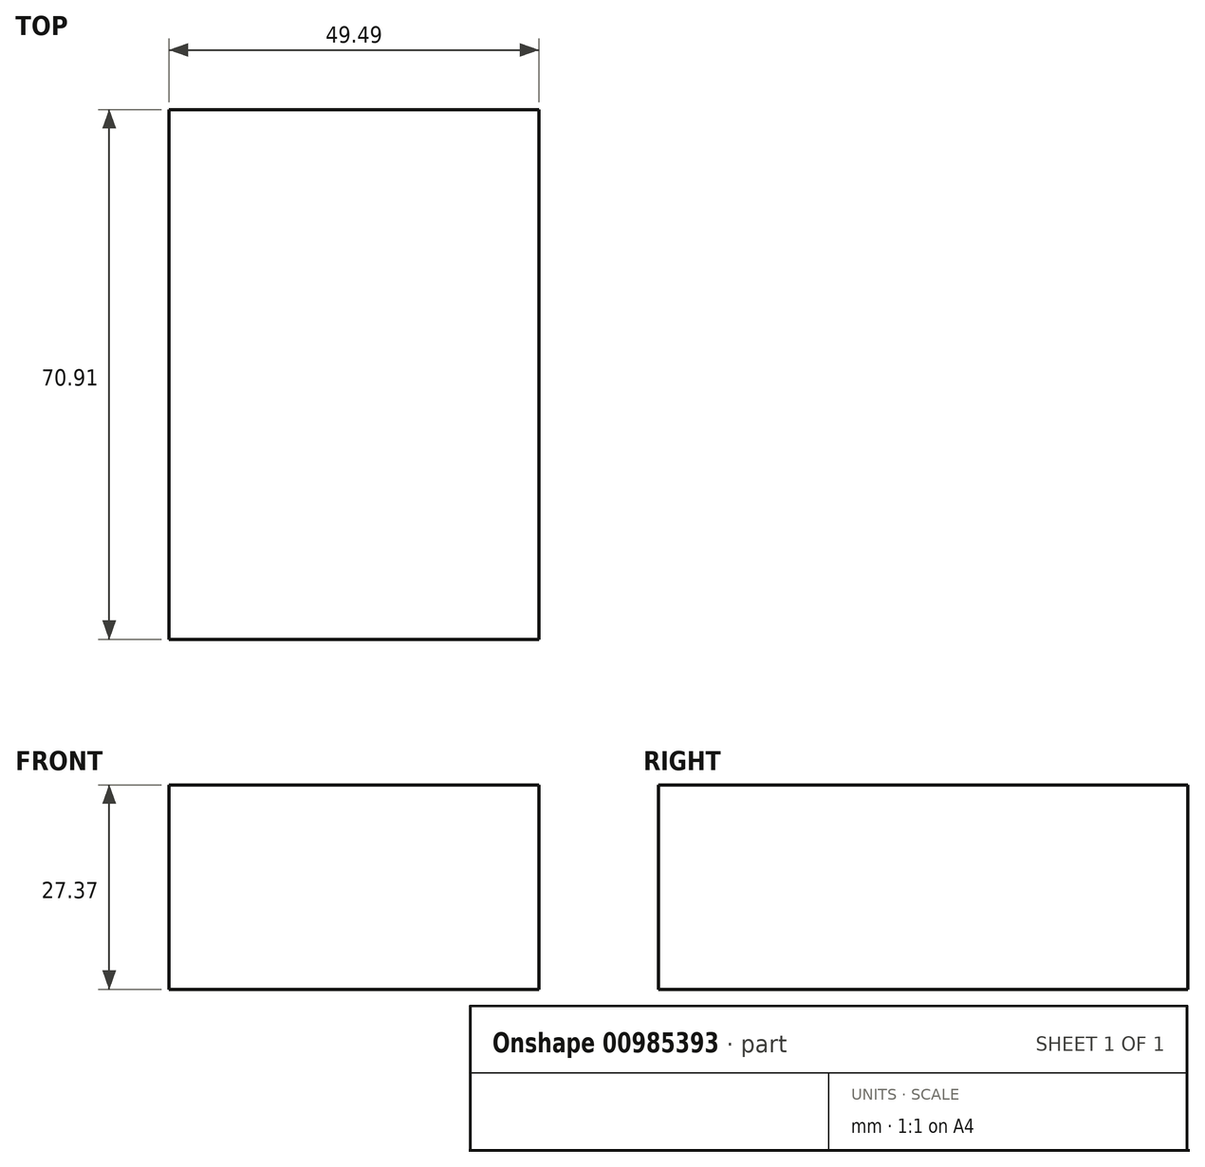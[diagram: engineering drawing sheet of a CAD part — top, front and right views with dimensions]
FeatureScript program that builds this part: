
annotation { "Feature Type Name" : "Feature", "Feature Type Description" : "" }
export const myFeature = defineFeature(function(context is Context, id is Id, definition is map)
    precondition{}
    {
        {
            var Q0;
            Q0=qCreatedBy(makeId("Front.planeOp"),FACE);
            var sketch = newSketch(context, id + "F0", { "sketchPlane" : qUnion([Q0])});
            skLineSegment(sketch, "E0.bottom", {"start": v(0, 0) * mm, "end": v(49.5, 0) * mm});
            skLineSegment(sketch, "E0.top", {"start": v(0, -27.37) * mm, "end": v(49.5, -27.37) * mm});
            skLineSegment(sketch, "E0.left", {"start": v(0, 0) * mm, "end": v(0, -27.37) * mm});
            skLineSegment(sketch, "E0.right", {"start": v(49.5, 0) * mm, "end": v(49.5, -27.37) * mm});
            skSolve(sketch);
        }
        {
            var Q0;
            Q0=makeQuery(id+"F0.imprint","IMPRINT",FACE,{"disambiguationData":[TD([[makeQuery(id+"F0.imprint","IMPRINT",EDGE,{"derivedFrom":sQuery(id+"F0.wireOp",EDGE,"E0.bottom")}),-1.0]])]});
            extrude(context, id + "F1", {"entities" : qUnion([Q0]), "depth" : 70.9 * mm, "offsetDistance" : 25.4 * mm});
        }
    });
